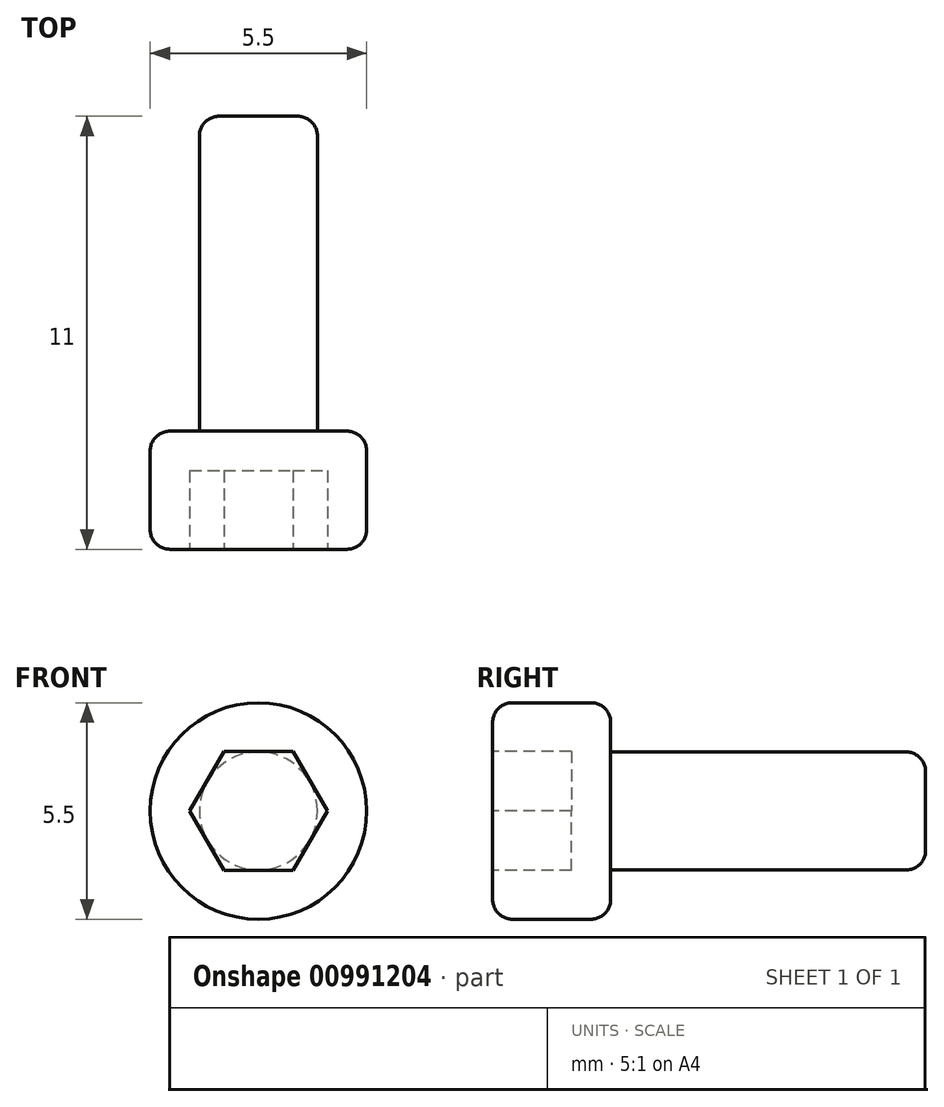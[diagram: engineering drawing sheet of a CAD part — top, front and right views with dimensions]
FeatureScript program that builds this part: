
annotation { "Feature Type Name" : "Feature", "Feature Type Description" : "" }
export const myFeature = defineFeature(function(context is Context, id is Id, definition is map)
    precondition{}
    {
        {
            var Q0;
            Q0=qCreatedBy(makeId("Front.planeOp"),FACE);
            var sketch = newSketch(context, id + "F0", { "sketchPlane" : qUnion([Q0])});
            skCircle(sketch, "E0", {"center": v(0, 0) * mm, "radius": 2.75 * mm});
            skSolve(sketch);
        }
        {
            var Q0;
            Q0=makeQuery(id+"F0.imprint","IMPRINT",FACE,{"disambiguationData":[TD([[makeQuery(id+"F0.imprint","IMPRINT",EDGE,{"derivedFrom":sQuery(id+"F0.wireOp",EDGE,"E0")}),1.0]])]});
            extrude(context, id + "F1", {"entities" : qUnion([Q0]), "depth" : 3 * mm, "offsetDistance" : 25 * mm});
        }
        {
            var Q0;
            Q0=makeQuery(id+"F1.opExtrude","CAP_FACE",FACE,{"disambiguationData":[OSD([sQuery(id+"F0.wireOp",EDGE,"E0")])],"isStart":false});
            var sketch = newSketch(context, id + "F2", { "sketchPlane" : qUnion([Q0])});
            skCircle(sketch, "E1", {"center": v(0, 0) * mm, "radius": 1.75 * mm});
            skCircle(sketch, "E2.cCircle", {"center": v(0, 0) * mm, "radius": 1.75 * mm, "construction": true});
            skLineSegment(sketch, "E2.0", {"start": v(-1.75, 0) * mm, "end": v(-0.88, 1.52) * mm});
            skLineSegment(sketch, "E2.1", {"start": v(-0.88, 1.52) * mm, "end": v(0.87, 1.52) * mm});
            skLineSegment(sketch, "E2.2", {"start": v(0.87, 1.52) * mm, "end": v(1.75, 0) * mm});
            skLineSegment(sketch, "E2.3", {"start": v(1.75, 0) * mm, "end": v(0.88, -1.52) * mm});
            skLineSegment(sketch, "E2.4", {"start": v(0.88, -1.52) * mm, "end": v(-0.87, -1.52) * mm});
            skLineSegment(sketch, "E2.5", {"start": v(-0.87, -1.52) * mm, "end": v(-1.75, 0) * mm});
            skSolve(sketch);
        }
        {
            var Q0;
            Q0=makeQuery(id+"F2.imprint","IMPRINT",FACE,{"disambiguationData":[TD([[makeQuery(id+"F2.imprint","IMPRINT",EDGE,{"derivedFrom":sQuery(id+"F2.wireOp",EDGE,"E2.0")}),-1.0]])]});
            extrude(context, id + "F3", {"entities" : qUnion([Q0]), "operationType" : NewBodyOperationType.REMOVE, "oppositeDirection" : true, "depth" : 2 * mm, "offsetDistance" : 25 * mm});
        }
        {
            var Q0;
            Q0=makeQuery(id+"F1.opExtrude","CAP_EDGE",EDGE,{"disambiguationData":[OSD([sQuery(id+"F0.wireOp",EDGE,"E0")])],"isStart":false});
            fillet(context, id + "F4", {"entities" : qUnion([Q0]), "radius" : 0.5 * mm, "tangentPropagation" : true, "allowEdgeOverflow" : false});
        }
        {
            var Q0;
            Q0=makeQuery(id+"F1.opExtrude","CAP_FACE",FACE,{"disambiguationData":[OSD([sQuery(id+"F0.wireOp",EDGE,"E0")])],"isStart":true});
            var sketch = newSketch(context, id + "F5", { "sketchPlane" : qUnion([Q0])});
            skCircle(sketch, "E3", {"center": v(0, 0) * mm, "radius": 1.5 * mm});
            skSolve(sketch);
        }
        {
            var Q0;
            Q0 = qSketchRegion(id + "F5", true);
            extrude(context, id + "F6", {"entities" : qUnion([Q0]), "operationType" : NewBodyOperationType.ADD, "depth" : 8 * mm, "offsetDistance" : 25 * mm});
        }
        {
            var Q0;
            Q0=makeQuery(id+"F1.opExtrude","CAP_EDGE",EDGE,{"disambiguationData":[OSD([sQuery(id+"F0.wireOp",EDGE,"E0")])],"isStart":true});
            fillet(context, id + "F7", {"entities" : qUnion([Q0]), "radius" : 0.5 * mm, "tangentPropagation" : true, "allowEdgeOverflow" : false});
        }
        {
            var Q0;
            Q0=makeQuery(id+"F6.opExtrude","CAP_EDGE",EDGE,{"disambiguationData":[OSD([sQuery(id+"F5.wireOp",EDGE,"E3")])],"isStart":false});
            fillet(context, id + "F8", {"entities" : qUnion([Q0]), "radius" : 0.5 * mm, "tangentPropagation" : true, "allowEdgeOverflow" : false});
        }
    });
